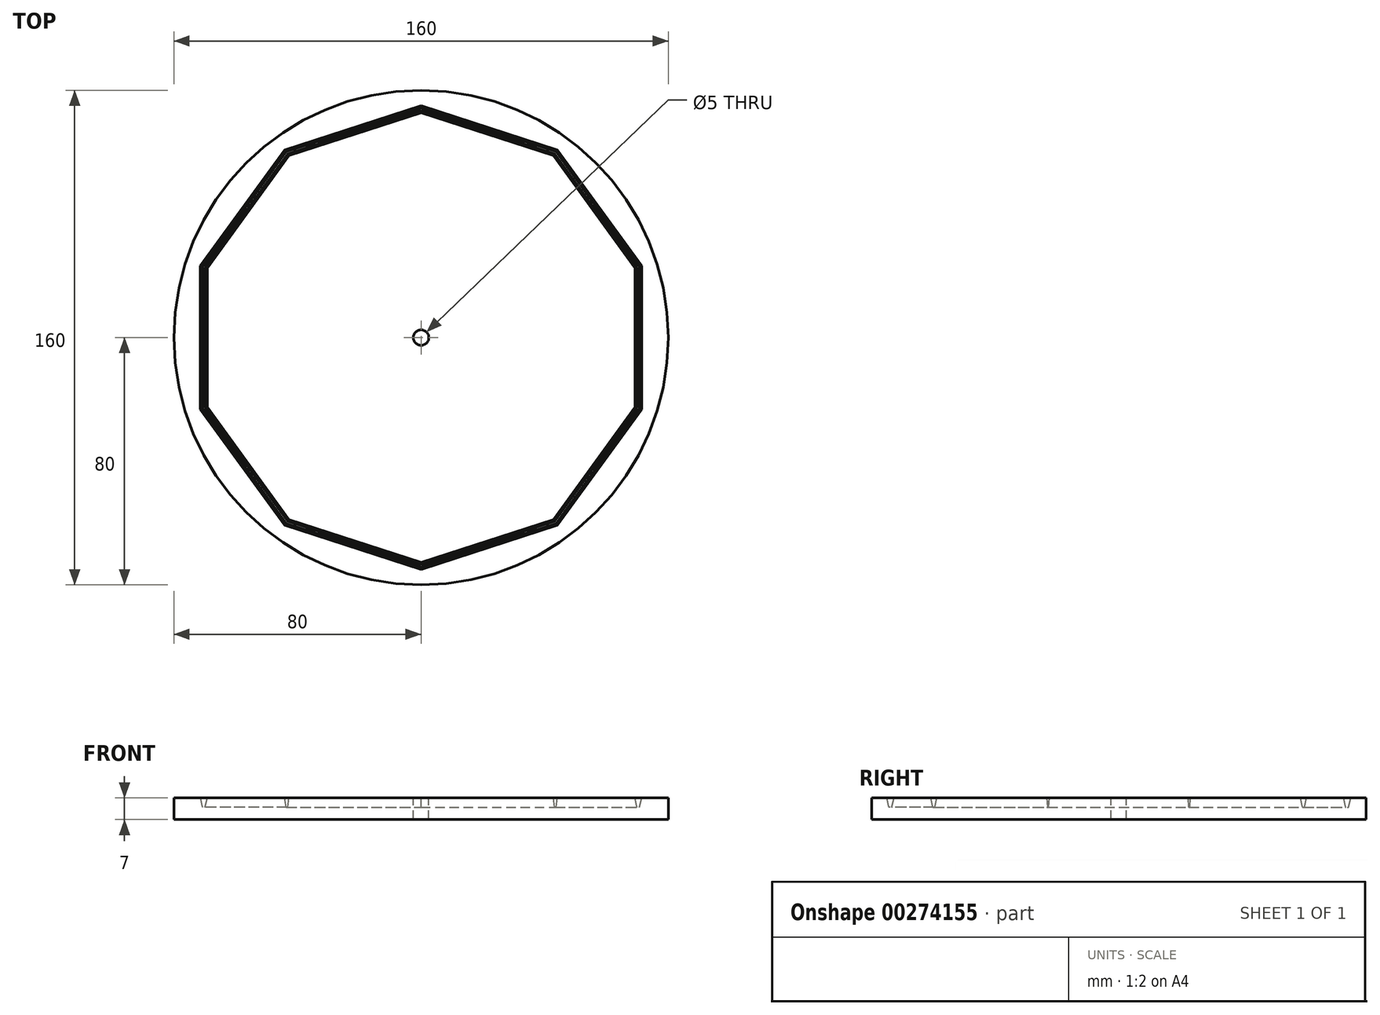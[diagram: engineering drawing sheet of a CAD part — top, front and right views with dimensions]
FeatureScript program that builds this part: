
annotation { "Feature Type Name" : "Feature", "Feature Type Description" : "" }
export const myFeature = defineFeature(function(context is Context, id is Id, definition is map)
    precondition{}
    {
        {
            var Q0;
            Q0=qCreatedBy(makeId("Top.planeOp"),FACE);
            var sketch = newSketch(context, id + "F0", { "sketchPlane" : qUnion([Q0])});
            skCircle(sketch, "E0", {"center": v(0, 0) * mm, "radius": 80 * mm});
            skCircle(sketch, "E1", {"center": v(0, 0) * mm, "radius": 2.5 * mm});
            skSolve(sketch);
        }
        {
            var Q0;
            Q0=makeQuery(id+"F0.imprint","IMPRINT",FACE,{"disambiguationData":[TD([[makeQuery(id+"F0.imprint","IMPRINT",EDGE,{"derivedFrom":sQuery(id+"F0.wireOp",EDGE,"E0")}),1.0]])]});
            extrude(context, id + "F1", {"entities" : qUnion([Q0]), "oppositeDirection" : true, "depth" : 7 * mm});
        }
        {
            var Q0;
            Q0=makeQuery(id+"F1.opExtrude","CAP_FACE",FACE,{"disambiguationData":[OSD([sQuery(id+"F0.wireOp",EDGE,"E0")])],"isStart":true});
            var sketch = newSketch(context, id + "F2", { "sketchPlane" : qUnion([Q0])});
            skCircle(sketch, "E2.cCircle", {"center": v(0, 0) * mm, "radius": 75.08 * mm, "construction": true});
            skLineSegment(sketch, "E2.0", {"start": v(0, -75.08) * mm, "end": v(-44.13, -60.74) * mm});
            skLineSegment(sketch, "E2.1", {"start": v(-44.13, -60.74) * mm, "end": v(-71.4, -23.2) * mm});
            skLineSegment(sketch, "E2.2", {"start": v(-71.4, -23.2) * mm, "end": v(-71.4, 23.2) * mm});
            skLineSegment(sketch, "E2.3", {"start": v(-71.4, 23.2) * mm, "end": v(-44.13, 60.74) * mm});
            skLineSegment(sketch, "E2.4", {"start": v(-44.13, 60.74) * mm, "end": v(0, 75.08) * mm});
            skLineSegment(sketch, "E2.5", {"start": v(0, 75.08) * mm, "end": v(44.13, 60.74) * mm});
            skLineSegment(sketch, "E2.6", {"start": v(44.13, 60.74) * mm, "end": v(71.4, 23.2) * mm});
            skLineSegment(sketch, "E2.7", {"start": v(71.4, 23.2) * mm, "end": v(71.4, -23.2) * mm});
            skLineSegment(sketch, "E2.8", {"start": v(71.4, -23.2) * mm, "end": v(44.13, -60.74) * mm});
            skLineSegment(sketch, "E2.9", {"start": v(44.13, -60.74) * mm, "end": v(0, -75.08) * mm});
            skLineSegment(sketch, "E3.0", {"start": v(-69.2, -22.49) * mm, "end": v(-69.2, 22.49) * mm});
            skLineSegment(sketch, "E3.1", {"start": v(-42.77, -58.87) * mm, "end": v(-69.2, -22.49) * mm});
            skLineSegment(sketch, "E3.2", {"start": v(-69.2, 22.49) * mm, "end": v(-42.77, 58.87) * mm});
            skLineSegment(sketch, "E3.3", {"start": v(0, -72.77) * mm, "end": v(-42.77, -58.87) * mm});
            skLineSegment(sketch, "E3.4", {"start": v(42.77, -58.87) * mm, "end": v(0, -72.77) * mm});
            skLineSegment(sketch, "E3.5", {"start": v(69.2, -22.49) * mm, "end": v(42.77, -58.87) * mm});
            skLineSegment(sketch, "E3.6", {"start": v(-42.77, 58.87) * mm, "end": v(0, 72.77) * mm});
            skLineSegment(sketch, "E3.7", {"start": v(0, 72.77) * mm, "end": v(42.77, 58.87) * mm});
            skLineSegment(sketch, "E3.8", {"start": v(42.77, 58.87) * mm, "end": v(69.2, 22.49) * mm});
            skLineSegment(sketch, "E3.9", {"start": v(69.2, 22.49) * mm, "end": v(69.2, -22.49) * mm});
            skSolve(sketch);
        }
        {
            var Q0;
            Q0=makeQuery(id+"F2.imprint","IMPRINT",FACE,{"disambiguationData":[TD([[makeQuery(id+"F2.imprint","IMPRINT",EDGE,{"derivedFrom":sQuery(id+"F2.wireOp",EDGE,"E2.0")}),-1.0]])]});
            extrude(context, id + "F3", {"entities" : qUnion([Q0]), "operationType" : NewBodyOperationType.REMOVE, "oppositeDirection" : true, "depth" : 3 * mm, "hasDraft" : true, "draftAngle" : 13.1 * degree, "draftPullDirection" : true});
        }
    });
